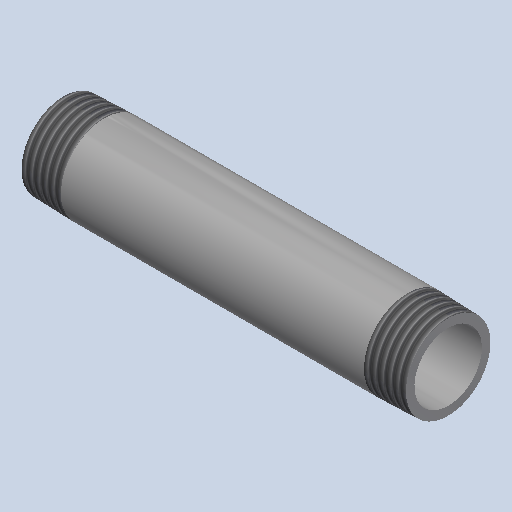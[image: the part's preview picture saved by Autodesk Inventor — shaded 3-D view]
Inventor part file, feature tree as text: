
AUTODESK INVENTOR PART (.ipt)
format: ipt  version: 2025 (Build 290162000, 162)  size: 215,040 bytes
history: native  units: mm (DEFAULTED — no unit token found)
features: other x8, revolve x1
ambient origin geometry x8: Origin, YZ Plane, XZ Plane, XY Plane, X Axis, Y Axis, Z Axis, Center Point
bodies: Solid1 (feature_tree)
feature tree (9):
  revolve  "Revolution1"  [1 undecoded]
  other  "Work Axis1"
  other  "Work Point5"
  other  "Work Axis2"
  other  "Work Point6"
  other  "Work Axis3"
  other  "Work Axis4"
  other  "Work Point7"
  other  "Work Point8"
note: 1 required parameter value undecoded (feature->parameter linkage not recoverable at this tier; creation-order binding heuristic only, values carry confidence <= 0.55)
